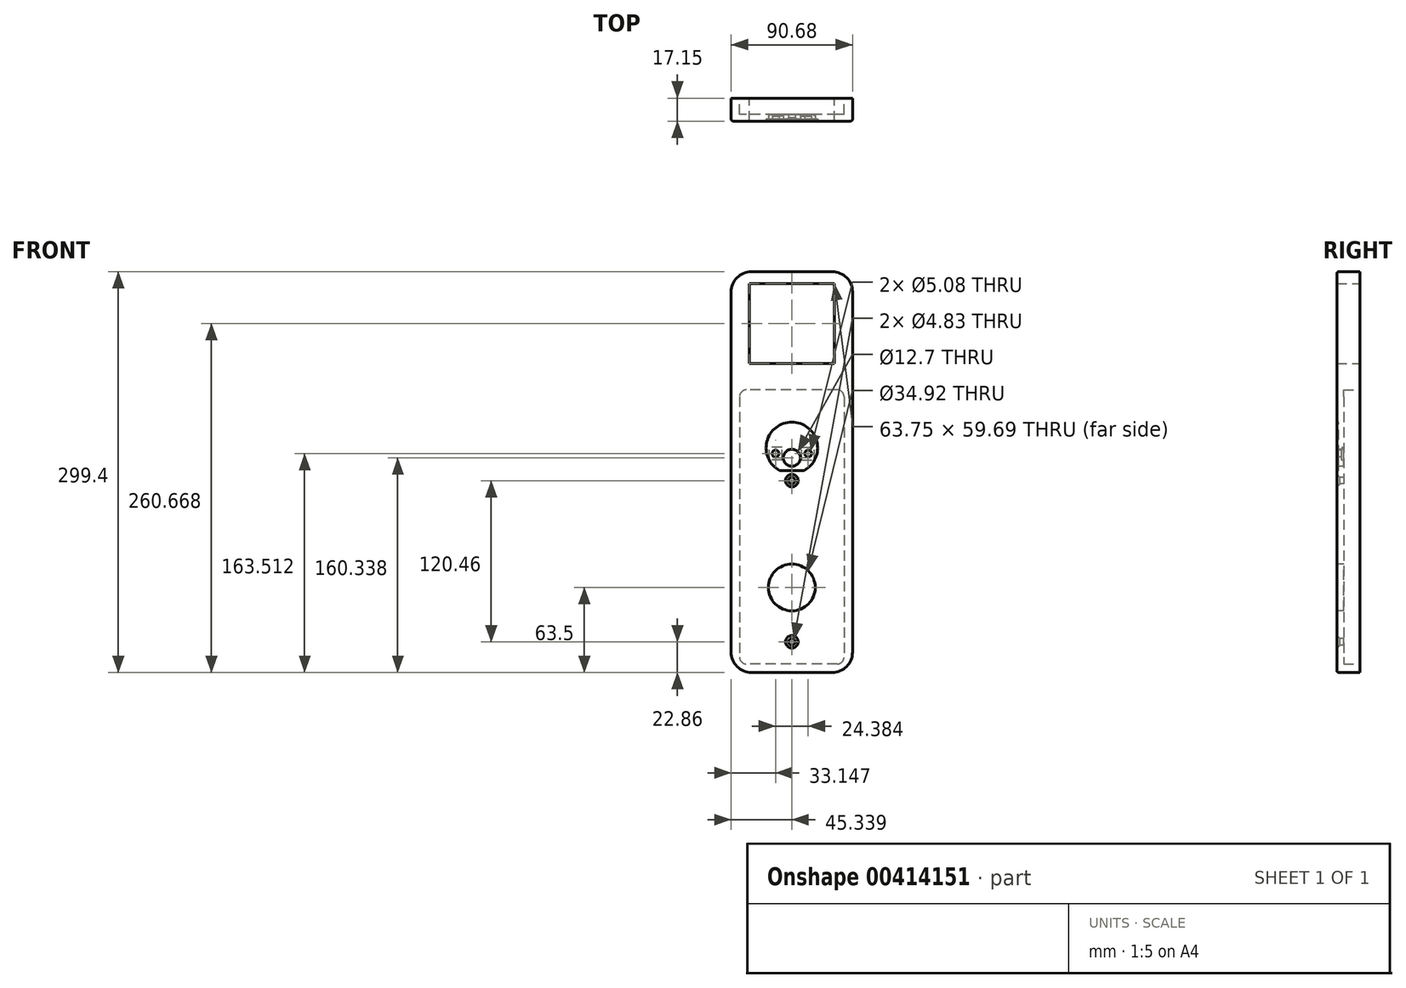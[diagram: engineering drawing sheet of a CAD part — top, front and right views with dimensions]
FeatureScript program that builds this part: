
annotation { "Feature Type Name" : "Feature", "Feature Type Description" : "" }
export const myFeature = defineFeature(function(context is Context, id is Id, definition is map)
    precondition{}
    {
        {
            var Q0;
            Q0=qCreatedBy(makeId("Front.planeOp"),FACE);
            var sketch = newSketch(context, id + "F0", { "sketchPlane" : qUnion([Q0])});
            skLineSegment(sketch, "E0.bottom", {"start": v(0, 0) * mm, "end": v(90.68, 0) * mm});
            skLineSegment(sketch, "E0.top", {"start": v(0, 217.49) * mm, "end": v(90.68, 217.49) * mm});
            skLineSegment(sketch, "E0.left", {"start": v(0, 0) * mm, "end": v(0, 217.49) * mm});
            skLineSegment(sketch, "E0.right", {"start": v(90.68, 0) * mm, "end": v(90.68, 217.49) * mm});
            skSolve(sketch);
        }
        {
            var Q0;
            Q0 = qSketchRegion(id + "F0", true);
            extrude(context, id + "F1", {"entities" : qUnion([Q0]), "depth" : 17.14 * mm});
        }
        {
            var Q0;
            Q0=makeQuery(id+"F1.opExtrude","CAP_FACE",FACE,{"disambiguationData":[OSD([sQuery(id+"F0.wireOp",EDGE,"E0.bottom"),sQuery(id+"F0.wireOp",EDGE,"E0.top"),sQuery(id+"F0.wireOp",EDGE,"E0.left"),sQuery(id+"F0.wireOp",EDGE,"E0.right")])],"isStart":false});
            var sketch = newSketch(context, id + "F2", { "sketchPlane" : qUnion([Q0])});
            skLineSegment(sketch, "E1", {"start": v(45.34, 0) * mm, "end": v(45.34, 217.49) * mm, "construction": true});
            skLineSegment(sketch, "E2.bottom", {"start": v(6.35, 211.14) * mm, "end": v(84.33, 211.14) * mm, "construction": true});
            skLineSegment(sketch, "E2.top", {"start": v(6.35, 6.35) * mm, "end": v(84.33, 6.35) * mm, "construction": true});
            skLineSegment(sketch, "E2.left", {"start": v(6.35, 211.14) * mm, "end": v(6.35, 6.35) * mm, "construction": true});
            skLineSegment(sketch, "E2.right", {"start": v(84.33, 211.14) * mm, "end": v(84.33, 6.35) * mm, "construction": true});
            skLineSegment(sketch, "E3", {"start": v(0, 63.5) * mm, "end": v(90.68, 63.5) * mm, "construction": true});
            skLineSegment(sketch, "E4", {"start": v(0, 160.34) * mm, "end": v(90.68, 160.34) * mm, "construction": true});
            skCircle(sketch, "E5", {"center": v(45.34, 160.34) * mm, "radius": 6.35 * mm});
            skCircle(sketch, "E6", {"center": v(45.34, 63.5) * mm, "radius": 17.46 * mm});
            skLineSegment(sketch, "E7", {"start": v(0, 22.86) * mm, "end": v(90.68, 22.86) * mm, "construction": true});
            skCircle(sketch, "E8", {"center": v(45.34, 22.86) * mm, "radius": 2.41 * mm});
            skLineSegment(sketch, "E9", {"start": v(0, 143.32) * mm, "end": v(90.68, 143.32) * mm, "construction": true});
            skCircle(sketch, "E10", {"center": v(45.34, 143.32) * mm, "radius": 2.41 * mm});
            skLineSegment(sketch, "E11", {"start": v(0, 167.77) * mm, "end": v(90.68, 167.77) * mm, "construction": true});
            skCircle(sketch, "E12", {"center": v(45.34, 167.77) * mm, "radius": 19.24 * mm});
            skLineSegment(sketch, "E13", {"start": v(36.24, 150.81) * mm, "end": v(54.44, 150.81) * mm});
            skLineSegment(sketch, "E14", {"start": v(0, 163.51) * mm, "end": v(90.68, 163.51) * mm, "construction": true});
            skCircle(sketch, "E15", {"center": v(57.53, 163.51) * mm, "radius": 2.54 * mm});
            skCircle(sketch, "E16", {"center": v(33.15, 163.51) * mm, "radius": 2.54 * mm});
            skSolve(sketch);
        }
        {
            var Q0;
            Q0=sQuery(id+"F2.wireOp",VERTEX,"E8.center");
            var Q1;
            Q1=makeQuery(id+"F1.opExtrude","SWEPT_BODY",BODY,{"disambiguationData":[OSD([sQuery(id+"F0.wireOp",EDGE,"E0.bottom"),sQuery(id+"F0.wireOp",EDGE,"E0.top"),sQuery(id+"F0.wireOp",EDGE,"E0.left"),sQuery(id+"F0.wireOp",EDGE,"E0.right")])]});
            hole(context, id + "F3", {"style" : HoleStyle.C_SINK, "endStyle" : HoleEndStyle.THROUGH, "holeDiameter" : 4.83 * mm, "cSinkDiameter" : 9.4 * mm, "cSinkAngle" : 84 * degree, "isTappedThrough" : true, "tappedDepth" : 12.7 * mm, "tapClearance" : 3, "locations" : qUnion([Q0]), "scope" : qUnion([Q1])});
        }
        {
            var Q0;
            Q0=makeQuery(id+"F2.imprint","IMPRINT",FACE,{"disambiguationData":[TD([[makeQuery(id+"F2.imprint","IMPRINT",EDGE,{"derivedFrom":sQuery(id+"F2.wireOp",EDGE,"E6")}),1.0]])]});
            var Q1;
            Q1=makeQuery(id+"F2.imprint","IMPRINT",FACE,{"disambiguationData":[TD([[makeQuery(id+"F2.imprint","IMPRINT",EDGE,{"derivedFrom":sQuery(id+"F2.wireOp",EDGE,"E5")}),1.0]])]});
            var Q2;
            Q2=makeQuery(id+"F2.imprint","IMPRINT",FACE,{"disambiguationData":[TD([[makeQuery(id+"F2.imprint","IMPRINT",EDGE,{"derivedFrom":sQuery(id+"F2.wireOp",EDGE,"E16")}),1.0]])]});
            var Q3;
            Q3=makeQuery(id+"F2.imprint","IMPRINT",FACE,{"disambiguationData":[TD([[makeQuery(id+"F2.imprint","IMPRINT",EDGE,{"derivedFrom":sQuery(id+"F2.wireOp",EDGE,"E15")}),1.0]])]});
            extrude(context, id + "F4", {"entities" : qUnion([Q0, Q1, Q2, Q3]), "operationType" : NewBodyOperationType.REMOVE, "oppositeDirection" : true, "depth" : 25.4 * mm});
        }
        {
            var Q0;
            Q0=makeQuery(id+"F1.opExtrude","CAP_FACE",FACE,{"disambiguationData":[OSD([sQuery(id+"F0.wireOp",EDGE,"E0.bottom"),sQuery(id+"F0.wireOp",EDGE,"E0.top"),sQuery(id+"F0.wireOp",EDGE,"E0.left"),sQuery(id+"F0.wireOp",EDGE,"E0.right")])],"isStart":true});
            var sketch = newSketch(context, id + "F5", { "sketchPlane" : qUnion([Q0])});
            skLineSegment(sketch, "E17.bottom", {"start": v(-84.33, 211.14) * mm, "end": v(-6.35, 211.14) * mm});
            skLineSegment(sketch, "E17.top", {"start": v(-84.33, 6.35) * mm, "end": v(-6.35, 6.35) * mm});
            skLineSegment(sketch, "E17.left", {"start": v(-84.33, 211.14) * mm, "end": v(-84.33, 6.35) * mm});
            skLineSegment(sketch, "E17.right", {"start": v(-6.35, 211.14) * mm, "end": v(-6.35, 6.35) * mm});
            skSolve(sketch);
        }
        {
            var Q0;
            Q0=makeQuery(id+"F5.imprint","IMPRINT",FACE,{"disambiguationData":[TD([[makeQuery(id+"F5.imprint","IMPRINT",EDGE,{"derivedFrom":sQuery(id+"F5.wireOp",EDGE,"E17.bottom")}),-1.0]])]});
            extrude(context, id + "F6", {"entities" : qUnion([Q0]), "operationType" : NewBodyOperationType.REMOVE, "oppositeDirection" : true, "depth" : 12.06 * mm});
        }
        {
            var Q0;
            Q0=sQuery(id+"F2.wireOp",VERTEX,"E10.center");
            var Q1;
            Q1=makeQuery(id+"F1.opExtrude","SWEPT_BODY",BODY,{"disambiguationData":[OSD([sQuery(id+"F0.wireOp",EDGE,"E0.bottom"),sQuery(id+"F0.wireOp",EDGE,"E0.top"),sQuery(id+"F0.wireOp",EDGE,"E0.left"),sQuery(id+"F0.wireOp",EDGE,"E0.right")])]});
            hole(context, id + "F7", {"style" : HoleStyle.C_SINK, "endStyle" : HoleEndStyle.THROUGH, "holeDiameter" : 4.83 * mm, "cSinkDiameter" : 9.4 * mm, "cSinkAngle" : 84 * degree, "isTappedThrough" : true, "tappedDepth" : 12.7 * mm, "tapClearance" : 3, "locations" : qUnion([Q0]), "scope" : qUnion([Q1])});
        }
        {
            var Q0;
            Q0=qCreatedBy(makeId("Front.planeOp"),FACE);
            var sketch = newSketch(context, id + "F8", { "sketchPlane" : qUnion([Q0])});
            skLineSegment(sketch, "E18.bottom", {"start": v(0, 217.49) * mm, "end": v(90.68, 217.49) * mm});
            skLineSegment(sketch, "E18.top", {"start": v(0, 299.4) * mm, "end": v(90.68, 299.4) * mm});
            skLineSegment(sketch, "E18.left", {"start": v(0, 217.49) * mm, "end": v(0, 299.4) * mm});
            skLineSegment(sketch, "E18.right", {"start": v(90.68, 217.49) * mm, "end": v(90.68, 299.4) * mm});
            skSolve(sketch);
        }
        {
            var Q0;
            Q0 = qSketchRegion(id + "F8", true);
            var Q1;
            Q1=makeQuery(id+"F1.opExtrude","CAP_FACE",FACE,{"disambiguationData":[OSD([sQuery(id+"F0.wireOp",EDGE,"E0.bottom"),sQuery(id+"F0.wireOp",EDGE,"E0.top"),sQuery(id+"F0.wireOp",EDGE,"E0.left"),sQuery(id+"F0.wireOp",EDGE,"E0.right")])],"isStart":false});
            extrude(context, id + "F9", {"entities" : qUnion([Q0]), "operationType" : NewBodyOperationType.ADD, "endBound" : BoundingType.UP_TO_SURFACE, "endBoundEntityFace" : qUnion([Q1]), "depth" : 25.4 * mm});
        }
        {
            var Q0;
            Q0=makeQuery(id+"F9.boolean.opBoolean","MERGE",FACE,{"derivedFrom":[makeQuery(id+"F1.opExtrude","CAP_FACE",FACE,{"disambiguationData":[OSD([sQuery(id+"F0.wireOp",EDGE,"E0.bottom"),sQuery(id+"F0.wireOp",EDGE,"E0.top"),sQuery(id+"F0.wireOp",EDGE,"E0.left"),sQuery(id+"F0.wireOp",EDGE,"E0.right")])],"isStart":true}),makeQuery(id+"F9.opExtrude","CAP_FACE",FACE,{"disambiguationData":[OSD([sQuery(id+"F8.wireOp",EDGE,"E18.bottom"),sQuery(id+"F8.wireOp",EDGE,"E18.top"),sQuery(id+"F8.wireOp",EDGE,"E18.left"),sQuery(id+"F8.wireOp",EDGE,"E18.right")])],"isStart":true})]});
            var sketch = newSketch(context, id + "F10", { "sketchPlane" : qUnion([Q0])});
            skLineSegment(sketch, "E19.bottom", {"start": v(-77.22, 290.51) * mm, "end": v(-13.46, 290.51) * mm});
            skLineSegment(sketch, "E19.top", {"start": v(-77.22, 230.82) * mm, "end": v(-13.46, 230.82) * mm});
            skLineSegment(sketch, "E19.left", {"start": v(-77.22, 290.51) * mm, "end": v(-77.22, 230.82) * mm});
            skLineSegment(sketch, "E19.right", {"start": v(-13.46, 290.51) * mm, "end": v(-13.46, 230.82) * mm});
            skSolve(sketch);
        }
        {
            var Q0;
            Q0=makeQuery(id+"F10.imprint","IMPRINT",FACE,{"disambiguationData":[TD([[makeQuery(id+"F10.imprint","IMPRINT",EDGE,{"derivedFrom":sQuery(id+"F10.wireOp",EDGE,"E19.bottom")}),-1.0]])]});
            extrude(context, id + "F11", {"entities" : qUnion([Q0]), "operationType" : NewBodyOperationType.REMOVE, "endBound" : BoundingType.THROUGH_ALL, "oppositeDirection" : true, "depth" : 25.4 * mm});
        }
        {
            var Q0;
            Q0=makeQuery(id+"F2.imprint","IMPRINT",FACE,{"disambiguationData":[TD([[makeQuery(id+"F2.imprint","IMPRINT",EDGE,{"derivedFrom":sQuery(id+"F2.wireOp",EDGE,"E5")}),-1.0]])]});
            extrude(context, id + "F12", {"entities" : qUnion([Q0]), "operationType" : NewBodyOperationType.REMOVE, "oppositeDirection" : true, "depth" : 1.52 * mm});
        }
        {
            var Q0;
            Q0=makeQuery(id+"F6.boolean.opBoolean","COPY",FACE,{"derivedFrom":makeQuery(id+"F6.opExtrude","CAP_FACE",FACE,{"disambiguationData":[OSD([sQuery(id+"F0.wireOp",EDGE,"E0.bottom"),sQuery(id+"F0.wireOp",EDGE,"E0.top"),sQuery(id+"F0.wireOp",EDGE,"E0.left"),sQuery(id+"F0.wireOp",EDGE,"E0.right"),sQuery(id+"F2.wireOp",EDGE,"E5"),sQuery(id+"F2.wireOp",EDGE,"E6"),sQuery(id+"F2.wireOp",EDGE,"E15"),sQuery(id+"F2.wireOp",EDGE,"E16"),sQuery(id+"F3.hole-0.sketch.wireOp",EDGE,"core_line_2"),sQuery(id+"F5.wireOp",EDGE,"E17.bottom"),sQuery(id+"F5.wireOp",EDGE,"E17.top"),sQuery(id+"F5.wireOp",EDGE,"E17.left"),sQuery(id+"F5.wireOp",EDGE,"E17.right")])],"isStart":false})});
            var sketch = newSketch(context, id + "F13", { "sketchPlane" : qUnion([Q0])});
            skLineSegment(sketch, "E20.bottom", {"start": v(-52.77, 158.75) * mm, "end": v(-62.3, 158.75) * mm});
            skLineSegment(sketch, "E20.top", {"start": v(-52.77, 168.28) * mm, "end": v(-62.3, 168.28) * mm});
            skLineSegment(sketch, "E20.left", {"start": v(-52.77, 158.75) * mm, "end": v(-52.77, 168.28) * mm});
            skLineSegment(sketch, "E20.right", {"start": v(-62.3, 158.75) * mm, "end": v(-62.3, 168.28) * mm});
            skPoint(sketch, "E20.middle", {"position": v(-57.53, 163.51) * mm});
            skLineSegment(sketch, "E21.MirrorCS", {"start": v(-28.38, 158.75) * mm, "end": v(-28.38, 168.28) * mm});
            skLineSegment(sketch, "E22.MirrorCS", {"start": v(-37.9, 158.75) * mm, "end": v(-37.9, 168.28) * mm});
            skLineSegment(sketch, "E23.MirrorCS", {"start": v(-37.9, 168.28) * mm, "end": v(-28.38, 168.28) * mm});
            skLineSegment(sketch, "E24.MirrorCS", {"start": v(-37.9, 158.75) * mm, "end": v(-28.38, 158.75) * mm});
            skPoint(sketch, "E25.MirrorP", {"position": v(-33.15, 163.51) * mm});
            skSolve(sketch);
        }
        {
            var Q0;
            Q0=makeQuery(id+"F13.imprint","IMPRINT",FACE,{"disambiguationData":[TD([[makeQuery(id+"F13.imprint","IMPRINT",EDGE,{"derivedFrom":sQuery(id+"F13.wireOp",EDGE,"E20.bottom")}),-1.0]])]});
            var Q1;
            Q1=makeQuery(id+"F13.imprint","IMPRINT",FACE,{"disambiguationData":[TD([[makeQuery(id+"F13.imprint","IMPRINT",EDGE,{"derivedFrom":sQuery(id+"F13.wireOp",EDGE,"E21.MirrorCS")}),1.0]])]});
            extrude(context, id + "F14", {"entities" : qUnion([Q0, Q1]), "operationType" : NewBodyOperationType.REMOVE, "oppositeDirection" : true, "depth" : 1.52 * mm});
        }
        {
            var Q0;
            Q0=makeQuery(id+"F6.boolean.opBoolean","COPY",EDGE,{"derivedFrom":makeQuery(id+"F6.opExtrude","SWEPT_EDGE",EDGE,{"disambiguationData":[OSD([sQuery(id+"F5.wireOp",EDGE,"E17.bottom"),sQuery(id+"F5.wireOp",EDGE,"E17.left")])]})});
            var Q1;
            Q1=makeQuery(id+"F6.boolean.opBoolean","COPY",EDGE,{"derivedFrom":makeQuery(id+"F6.opExtrude","SWEPT_EDGE",EDGE,{"disambiguationData":[OSD([sQuery(id+"F5.wireOp",EDGE,"E17.bottom"),sQuery(id+"F5.wireOp",EDGE,"E17.right")])]})});
            var Q2;
            Q2=makeQuery(id+"F6.boolean.opBoolean","COPY",EDGE,{"derivedFrom":makeQuery(id+"F6.opExtrude","SWEPT_EDGE",EDGE,{"disambiguationData":[OSD([sQuery(id+"F5.wireOp",EDGE,"E17.top"),sQuery(id+"F5.wireOp",EDGE,"E17.right")])]})});
            var Q3;
            Q3=makeQuery(id+"F6.boolean.opBoolean","COPY",EDGE,{"derivedFrom":makeQuery(id+"F6.opExtrude","SWEPT_EDGE",EDGE,{"disambiguationData":[OSD([sQuery(id+"F5.wireOp",EDGE,"E17.top"),sQuery(id+"F5.wireOp",EDGE,"E17.left")])]})});
            fillet(context, id + "F15", {"entities" : qUnion([Q0, Q1, Q2, Q3]), "radius" : 5.08 * mm, "tangentPropagation" : true, "allowEdgeOverflow" : false});
        }
        {
            var Q0;
            Q0=makeQuery(id+"F1.opExtrude","SWEPT_EDGE",EDGE,{"disambiguationData":[OSD([sQuery(id+"F0.wireOp",EDGE,"E0.bottom"),sQuery(id+"F0.wireOp",EDGE,"E0.right")])]});
            var Q1;
            Q1=makeQuery(id+"F1.opExtrude","SWEPT_EDGE",EDGE,{"disambiguationData":[OSD([sQuery(id+"F0.wireOp",EDGE,"E0.bottom"),sQuery(id+"F0.wireOp",EDGE,"E0.left")])]});
            var Q2;
            Q2=makeQuery(id+"FjDSDH5W8p0qFOM_1.boolean.opBoolean","COPY",EDGE,{"derivedFrom":makeQuery(id+"FjDSDH5W8p0qFOM_1.opExtrude","SWEPT_EDGE",EDGE,{"disambiguationData":[OSD([sQuery(id+"FE6kahgUhfX9q7h_1.wireOp",EDGE,"oJ8mBncu-0kBl-iUJ4-Wzks-U8IMdtLDwv2D.top"),sQuery(id+"FE6kahgUhfX9q7h_1.wireOp",EDGE,"oJ8mBncu-0kBl-iUJ4-Wzks-U8IMdtLDwv2D.right")])]})});
            var Q3;
            Q3=makeQuery(id+"FjDSDH5W8p0qFOM_1.boolean.opBoolean","COPY",EDGE,{"derivedFrom":makeQuery(id+"FjDSDH5W8p0qFOM_1.opExtrude","SWEPT_EDGE",EDGE,{"disambiguationData":[OSD([sQuery(id+"FE6kahgUhfX9q7h_1.wireOp",EDGE,"oJ8mBncu-0kBl-iUJ4-Wzks-U8IMdtLDwv2D.top"),sQuery(id+"FE6kahgUhfX9q7h_1.wireOp",EDGE,"oJ8mBncu-0kBl-iUJ4-Wzks-U8IMdtLDwv2D.left")])]})});
            var Q4;
            Q4=makeQuery(id+"F9.opExtrude","SWEPT_EDGE",EDGE,{"disambiguationData":[OSD([sQuery(id+"F8.wireOp",EDGE,"E18.top"),sQuery(id+"F8.wireOp",EDGE,"E18.left")])]});
            var Q5;
            Q5=makeQuery(id+"F9.opExtrude","SWEPT_EDGE",EDGE,{"disambiguationData":[OSD([sQuery(id+"F8.wireOp",EDGE,"E18.top"),sQuery(id+"F8.wireOp",EDGE,"E18.right")])]});
            fillet(context, id + "F16", {"entities" : qUnion([Q0, Q1, Q2, Q3, Q4, Q5]), "radius" : 15.24 * mm, "tangentPropagation" : true, "allowEdgeOverflow" : false});
        }
        {
            var Q0;
            {var subQ0=sQuery(id+"F0.wireOp",EDGE,"E0.left");Q0=makeQuery(id+"F9.boolean.opBoolean","MERGE",EDGE,{"derivedFrom":[makeQuery(id+"F1.opExtrude","CAP_EDGE",EDGE,{"disambiguationData":[OSD([subQ0])],"isStart":false}),makeQuery(id+"F9.opExtrude","TWEAK_EDGE",EDGE,{"derivedFrom":[makeQuery(id+"F1.opExtrude","CAP_FACE",FACE,{"disambiguationData":[OSD([sQuery(id+"F0.wireOp",EDGE,"E0.bottom"),sQuery(id+"F0.wireOp",EDGE,"E0.top"),subQ0,sQuery(id+"F0.wireOp",EDGE,"E0.right")])],"isStart":false}),makeQuery(id+"F8.imprint","IMPRINT",EDGE,{"derivedFrom":sQuery(id+"F8.wireOp",EDGE,"E18.left")})]})]});}
            fillet(context, id + "F17", {"entities" : qUnion([Q0]), "radius" : 1.59 * mm, "tangentPropagation" : true, "allowEdgeOverflow" : false});
        }
    });
